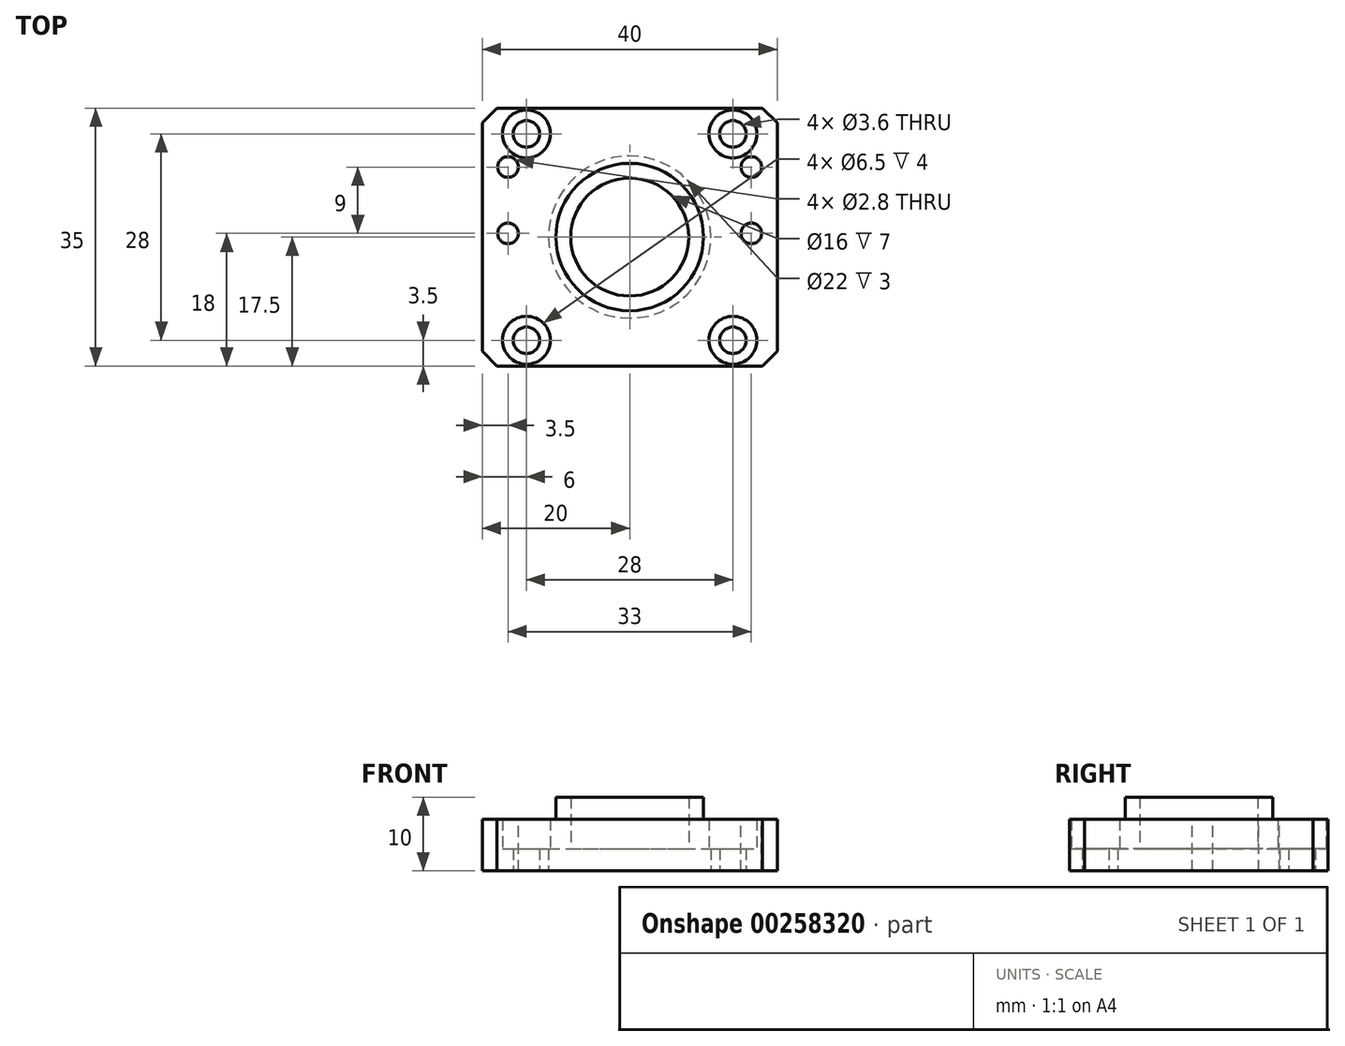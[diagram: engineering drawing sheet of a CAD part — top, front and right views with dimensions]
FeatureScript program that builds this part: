
annotation { "Feature Type Name" : "Feature", "Feature Type Description" : "" }
export const myFeature = defineFeature(function(context is Context, id is Id, definition is map)
    precondition{}
    {
        {
            var Q0;
            Q0=qCreatedBy(makeId("Top.planeOp"),FACE);
            var sketch = newSketch(context, id + "F0", { "sketchPlane" : qUnion([Q0])});
            skLineSegment(sketch, "E0.bottom", {"start": v(20, 17.5) * mm, "end": v(-20, 17.5) * mm, "construction": true});
            skLineSegment(sketch, "E0.top", {"start": v(20, -17.5) * mm, "end": v(-20, -17.5) * mm, "construction": true});
            skLineSegment(sketch, "E0.left", {"start": v(20, 17.5) * mm, "end": v(20, -17.5) * mm, "construction": true});
            skLineSegment(sketch, "E0.right", {"start": v(-20, 17.5) * mm, "end": v(-20, -17.5) * mm, "construction": true});
            skPoint(sketch, "E0.middle", {"position": v(0, 0) * mm});
            skCircle(sketch, "E1", {"center": v(0, 0) * mm, "radius": 11 * mm, "construction": true});
            skCircle(sketch, "E2", {"center": v(0, 0) * mm, "radius": 8 * mm, "construction": true});
            skCircle(sketch, "E3", {"center": v(0, 0) * mm, "radius": 10 * mm, "construction": true});
            skLineSegment(sketch, "E4.bottom", {"start": v(14, -14) * mm, "end": v(-14, -14) * mm, "construction": true});
            skLineSegment(sketch, "E4.top", {"start": v(14, 14) * mm, "end": v(-14, 14) * mm, "construction": true});
            skLineSegment(sketch, "E4.left", {"start": v(14, -14) * mm, "end": v(14, 14) * mm, "construction": true});
            skLineSegment(sketch, "E4.right", {"start": v(-14, -14) * mm, "end": v(-14, 14) * mm, "construction": true});
            skLineSegment(sketch, "E5.bottom", {"start": v(-16.5, 9.5) * mm, "end": v(16.5, 9.5) * mm, "construction": true});
            skLineSegment(sketch, "E5.top", {"start": v(-16.5, 0.5) * mm, "end": v(16.5, 0.5) * mm, "construction": true});
            skLineSegment(sketch, "E5.left", {"start": v(-16.5, 9.5) * mm, "end": v(-16.5, 0.5) * mm, "construction": true});
            skLineSegment(sketch, "E5.right", {"start": v(16.5, 9.5) * mm, "end": v(16.5, 0.5) * mm, "construction": true});
            skLineSegment(sketch, "E6", {"start": v(0, 17.5) * mm, "end": v(0, -17.5) * mm, "construction": true});
            skPoint(sketch, "E7", {"position": v(0, 0.5) * mm});
            skSolve(sketch);
        }
        {
            var Q0;
            Q0=qCreatedBy(makeId("Top.planeOp"),FACE);
            var sketch = newSketch(context, id + "F1", { "sketchPlane" : qUnion([Q0])});
            skLineSegment(sketch, "E8.0", {"start": v(20, 17.5) * mm, "end": v(-20, 17.5) * mm});
            skLineSegment(sketch, "E8.1", {"start": v(20, 17.5) * mm, "end": v(20, -17.5) * mm});
            skLineSegment(sketch, "E8.2", {"start": v(20, -17.5) * mm, "end": v(-20, -17.5) * mm});
            skLineSegment(sketch, "E8.3", {"start": v(-20, 17.5) * mm, "end": v(-20, -17.5) * mm});
            skSolve(sketch);
        }
        {
            var Q0;
            Q0 = qSketchRegion(id + "F1", true);
            var Q1;
            Q1 = qConstructionFilter(qBodyType(qCreatedBy(id + "F1" ,EDGE), BodyType.WIRE), ConstructionObject.NO);
            extrude(context, id + "F2", {"entities" : qUnion([Q0]), "surfaceEntities" : qUnion([Q1]), "depth" : 7 * mm, "offsetDistance" : 25 * mm});
        }
        {
            var Q0;
            Q0=makeQuery(id+"F2.opExtrude","CAP_FACE",FACE,{"disambiguationData":[OSD([sQuery(id+"F1.wireOp",EDGE,"E8.0"),sQuery(id+"F1.wireOp",EDGE,"E8.1"),sQuery(id+"F1.wireOp",EDGE,"E8.2"),sQuery(id+"F1.wireOp",EDGE,"E8.3")])],"isStart":false});
            var sketch = newSketch(context, id + "F3", { "sketchPlane" : qUnion([Q0])});
            skCircle(sketch, "E9.0", {"center": v(0, 0) * mm, "radius": 8 * mm});
            skCircle(sketch, "E9.1", {"center": v(0, 0) * mm, "radius": 10 * mm});
            skSolve(sketch);
        }
        {
            var Q0;
            Q0 = qSketchRegion(id + "F3", true);
            extrude(context, id + "F4", {"entities" : qUnion([Q0]), "operationType" : NewBodyOperationType.ADD, "depth" : 3 * mm, "offsetDistance" : 25 * mm});
        }
        {
            var Q0;
            Q0=makeQuery(id+"F4.boolean.opBoolean","SPLIT",FACE,{"disambiguationData":[TD([makeQuery(id+"F4.opExtrude","SWEPT_FACE",FACE,{"disambiguationData":[OSD([sQuery(id+"F3.wireOp",EDGE,"E9.0")])]})])],"derivedFrom":makeQuery(id+"F2.opExtrude","CAP_FACE",FACE,{"disambiguationData":[OSD([sQuery(id+"F1.wireOp",EDGE,"E8.0"),sQuery(id+"F1.wireOp",EDGE,"E8.1"),sQuery(id+"F1.wireOp",EDGE,"E8.2"),sQuery(id+"F1.wireOp",EDGE,"E8.3")])],"isStart":false})});
            extrude(context, id + "F5", {"entities" : qUnion([Q0]), "operationType" : NewBodyOperationType.REMOVE, "endBound" : BoundingType.UP_TO_NEXT, "oppositeDirection" : true, "depth" : 25 * mm, "offsetDistance" : 25 * mm});
        }
        {
            var Q0;
            Q0=makeQuery(id+"F2.opExtrude","CAP_FACE",FACE,{"disambiguationData":[OSD([sQuery(id+"F1.wireOp",EDGE,"E8.0"),sQuery(id+"F1.wireOp",EDGE,"E8.1"),sQuery(id+"F1.wireOp",EDGE,"E8.2"),sQuery(id+"F1.wireOp",EDGE,"E8.3")])],"isStart":true});
            var sketch = newSketch(context, id + "F6", { "sketchPlane" : qUnion([Q0])});
            skCircle(sketch, "E10.0", {"center": v(0, 0) * mm, "radius": 11 * mm});
            skSolve(sketch);
        }
        {
            var Q0;
            Q0 = qSketchRegion(id + "F6", true);
            extrude(context, id + "F7", {"entities" : qUnion([Q0]), "operationType" : NewBodyOperationType.REMOVE, "oppositeDirection" : true, "depth" : 3 * mm, "offsetDistance" : 25 * mm});
        }
        {
            var Q0;
            {var subQ0=sQuery(id+"F1.wireOp",EDGE,"E8.2");var subQ1=sQuery(id+"F1.wireOp",EDGE,"E8.1");var subQ2=sQuery(id+"F1.wireOp",EDGE,"E8.3");var subQ3=sQuery(id+"F1.wireOp",EDGE,"E8.0");Q0=makeQuery(id+"F4.boolean.opBoolean","SPLIT",FACE,{"disambiguationData":[TD([makeQuery(id+"F2.opExtrude","SWEPT_FACE",FACE,{"disambiguationData":[OSD([subQ3])]})])],"derivedFrom":makeQuery(id+"F2.opExtrude","CAP_FACE",FACE,{"disambiguationData":[OSD([subQ3,subQ1,subQ0,subQ2])],"isStart":false})});}
            var sketch = newSketch(context, id + "F8", { "sketchPlane" : qUnion([Q0])});
            skLineSegment(sketch, "E11.0", {"start": v(14, -14) * mm, "end": v(-14, -14) * mm, "construction": true});
            skLineSegment(sketch, "E11.1", {"start": v(-14, -14) * mm, "end": v(-14, 14) * mm, "construction": true});
            skLineSegment(sketch, "E11.2", {"start": v(14, 14) * mm, "end": v(-14, 14) * mm, "construction": true});
            skLineSegment(sketch, "E11.3", {"start": v(14, -14) * mm, "end": v(14, 14) * mm, "construction": true});
            skSolve(sketch);
        }
        {
            var Q0;
            Q0=sQuery(id+"F8.wireOp",VERTEX,"E11.2.end");
            var Q1;
            Q1=sQuery(id+"F8.wireOp",VERTEX,"E11.3.end");
            var Q2;
            Q2=sQuery(id+"F8.wireOp",VERTEX,"E11.0.start");
            var Q3;
            Q3=sQuery(id+"F8.wireOp",VERTEX,"E11.1.start");
            var Q4;
            Q4=makeQuery(id+"F2.opExtrude","SWEPT_BODY",BODY,{"disambiguationData":[OSD([sQuery(id+"F1.wireOp",EDGE,"E8.0"),sQuery(id+"F1.wireOp",EDGE,"E8.1"),sQuery(id+"F1.wireOp",EDGE,"E8.2"),sQuery(id+"F1.wireOp",EDGE,"E8.3")])]});
            hole(context, id + "F9", {"style" : HoleStyle.C_BORE, "endStyle" : HoleEndStyle.THROUGH, "holeDiameter" : 3.6 * mm, "cBoreDiameter" : 6.5 * mm, "cBoreDepth" : 4 * mm, "isTappedThrough" : true, "tappedDepth" : 12 * mm, "tapClearance" : 3, "locations" : qUnion([Q0, Q1, Q2, Q3]), "scope" : qUnion([Q4]), "startStyle" : HoleStartStyle.PART});
        }
        {
            var Q0;
            Q0=sQuery(id+"F0.wireOp",VERTEX,"E5.bottom.start");
            var Q1;
            Q1=sQuery(id+"F0.wireOp",VERTEX,"E5.top.start");
            var Q2;
            Q2=sQuery(id+"F0.wireOp",VERTEX,"E5.right.start");
            var Q3;
            Q3=sQuery(id+"F0.wireOp",VERTEX,"E5.right.end");
            var Q4;
            Q4=makeQuery(id+"F2.opExtrude","SWEPT_BODY",BODY,{"disambiguationData":[OSD([sQuery(id+"F1.wireOp",EDGE,"E8.0"),sQuery(id+"F1.wireOp",EDGE,"E8.1"),sQuery(id+"F1.wireOp",EDGE,"E8.2"),sQuery(id+"F1.wireOp",EDGE,"E8.3")])]});
            hole(context, id + "F10", {"style" : HoleStyle.SIMPLE, "endStyle" : HoleEndStyle.THROUGH, "oppositeDirection" : true, "holeDiameter" : 2.8 * mm, "isTappedThrough" : true, "tappedDepth" : 12 * mm, "tapClearance" : 3, "locations" : qUnion([Q0, Q1, Q2, Q3]), "scope" : qUnion([Q4]), "startStyle" : HoleStartStyle.PART});
        }
        {
            var Q0;
            Q0=makeQuery(id+"F2.opExtrude","SWEPT_EDGE",EDGE,{"disambiguationData":[OSD([sQuery(id+"F1.wireOp",EDGE,"E8.0"),sQuery(id+"F1.wireOp",EDGE,"E8.3")])]});
            var Q1;
            Q1=makeQuery(id+"F2.opExtrude","SWEPT_EDGE",EDGE,{"disambiguationData":[OSD([sQuery(id+"F1.wireOp",EDGE,"E8.2"),sQuery(id+"F1.wireOp",EDGE,"E8.3")])]});
            var Q2;
            Q2=makeQuery(id+"F2.opExtrude","SWEPT_EDGE",EDGE,{"disambiguationData":[OSD([sQuery(id+"F1.wireOp",EDGE,"E8.0"),sQuery(id+"F1.wireOp",EDGE,"E8.1")])]});
            var Q3;
            Q3=makeQuery(id+"F2.opExtrude","SWEPT_EDGE",EDGE,{"disambiguationData":[OSD([sQuery(id+"F1.wireOp",EDGE,"E8.1"),sQuery(id+"F1.wireOp",EDGE,"E8.2")])]});
            chamfer(context, id + "F11", {"entities" : qUnion([Q0, Q1, Q2, Q3]), "width" : 2 * mm, "tangentPropagation" : true});
        }
    });
